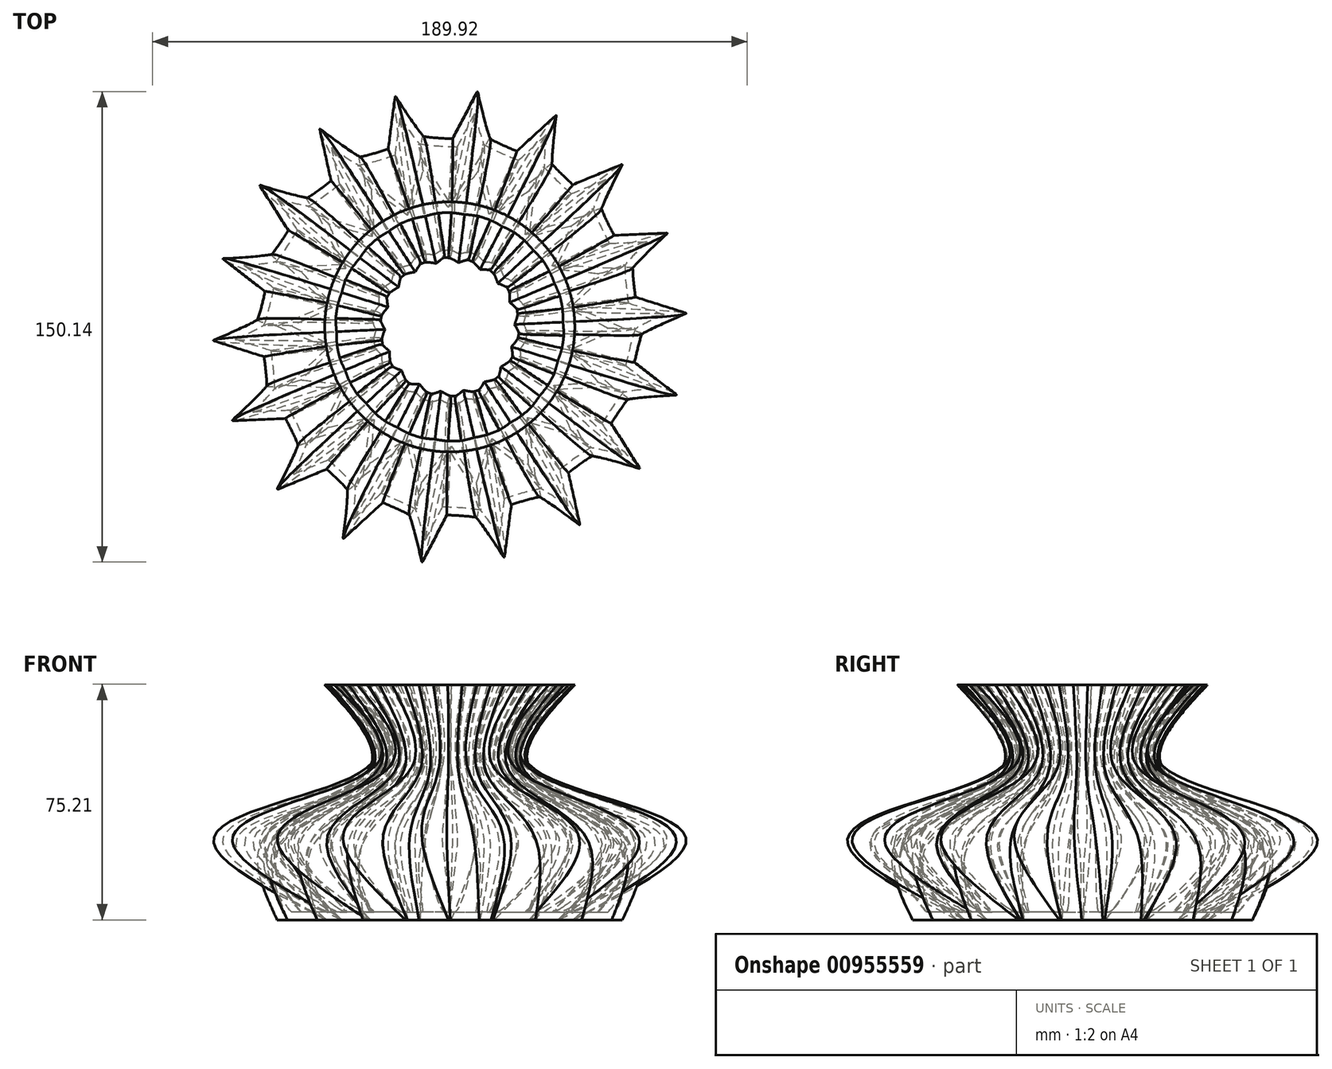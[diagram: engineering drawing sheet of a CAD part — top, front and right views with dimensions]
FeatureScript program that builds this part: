
annotation { "Feature Type Name" : "Feature", "Feature Type Description" : "" }
export const myFeature = defineFeature(function(context is Context, id is Id, definition is map)
    precondition{}
    {
        {
            var Q0;
            Q0=qCreatedBy(makeId("Top.planeOp"),FACE);
            var sketch = newSketch(context, id + "F0", { "sketchPlane" : qUnion([Q0])});
            skCircle(sketch, "E0", {"center": v(0, 0) * mm, "radius": 40 * mm});
            skLineSegment(sketch, "E1", {"start": v(-13.84, 37.53) * mm, "end": v(-27.36, 47.83) * mm});
            skLineSegment(sketch, "E2", {"start": v(-27.36, 47.83) * mm, "end": v(-25.33, 30.96) * mm});
            skLineSegment(sketch, "E3.1.0", {"start": v(-25.84, 30.53) * mm, "end": v(-42.07, 35.59) * mm});
            skLineSegment(sketch, "E3.1.1", {"start": v(-42.07, 35.59) * mm, "end": v(-34.4, 20.42) * mm});
            skLineSegment(sketch, "E3.2.0", {"start": v(-34.73, 19.85) * mm, "end": v(-51.7, 19.05) * mm});
            skLineSegment(sketch, "E3.2.1", {"start": v(-51.7, 19.05) * mm, "end": v(-39.3, 7.43) * mm});
            skLineSegment(sketch, "E3.3.0", {"start": v(-39.42, 6.78) * mm, "end": v(-55.1, 0.22) * mm});
            skLineSegment(sketch, "E3.3.1", {"start": v(-55.1, 0.22) * mm, "end": v(-39.47, -6.46) * mm});
            skLineSegment(sketch, "E3.4.0", {"start": v(-39.36, -7.12) * mm, "end": v(-51.86, -18.64) * mm});
            skLineSegment(sketch, "E3.4.1", {"start": v(-51.86, -18.64) * mm, "end": v(-34.88, -19.57) * mm});
            skLineSegment(sketch, "E3.5.0", {"start": v(-34.55, -20.15) * mm, "end": v(-42.36, -35.25) * mm});
            skLineSegment(sketch, "E3.5.1", {"start": v(-42.36, -35.25) * mm, "end": v(-26.09, -30.32) * mm});
            skLineSegment(sketch, "E3.6.0", {"start": v(-25.58, -30.75) * mm, "end": v(-27.74, -47.61) * mm});
            skLineSegment(sketch, "E3.6.1", {"start": v(-27.74, -47.61) * mm, "end": v(-14.14, -37.42) * mm});
            skLineSegment(sketch, "E3.7.0", {"start": v(-13.52, -37.65) * mm, "end": v(-9.78, -54.23) * mm});
            skLineSegment(sketch, "E3.7.1", {"start": v(-9.78, -54.23) * mm, "end": v(-0.5, -40) * mm});
            skLineSegment(sketch, "E3.8.0", {"start": v(0.17, -40) * mm, "end": v(9.35, -54.3) * mm});
            skLineSegment(sketch, "E3.8.1", {"start": v(9.35, -54.3) * mm, "end": v(13.22, -37.75) * mm});
            skLineSegment(sketch, "E3.9.0", {"start": v(13.84, -37.53) * mm, "end": v(27.36, -47.83) * mm});
            skLineSegment(sketch, "E3.9.1", {"start": v(27.36, -47.83) * mm, "end": v(25.33, -30.96) * mm});
            skLineSegment(sketch, "E3.10.0", {"start": v(25.84, -30.53) * mm, "end": v(42.07, -35.59) * mm});
            skLineSegment(sketch, "E3.10.1", {"start": v(42.07, -35.59) * mm, "end": v(34.4, -20.42) * mm});
            skLineSegment(sketch, "E3.11.0", {"start": v(34.73, -19.85) * mm, "end": v(51.7, -19.05) * mm});
            skLineSegment(sketch, "E3.11.1", {"start": v(51.7, -19.05) * mm, "end": v(39.3, -7.43) * mm});
            skLineSegment(sketch, "E3.12.0", {"start": v(39.42, -6.78) * mm, "end": v(55.1, -0.22) * mm});
            skLineSegment(sketch, "E3.12.1", {"start": v(55.1, -0.22) * mm, "end": v(39.47, 6.46) * mm});
            skLineSegment(sketch, "E3.13.0", {"start": v(39.36, 7.12) * mm, "end": v(51.86, 18.64) * mm});
            skLineSegment(sketch, "E3.13.1", {"start": v(51.86, 18.64) * mm, "end": v(34.88, 19.57) * mm});
            skLineSegment(sketch, "E3.14.0", {"start": v(34.55, 20.15) * mm, "end": v(42.36, 35.25) * mm});
            skLineSegment(sketch, "E3.14.1", {"start": v(42.36, 35.25) * mm, "end": v(26.09, 30.32) * mm});
            skLineSegment(sketch, "E3.15.0", {"start": v(25.58, 30.75) * mm, "end": v(27.74, 47.61) * mm});
            skLineSegment(sketch, "E3.15.1", {"start": v(27.74, 47.61) * mm, "end": v(14.14, 37.42) * mm});
            skLineSegment(sketch, "E3.16.0", {"start": v(13.52, 37.65) * mm, "end": v(9.78, 54.23) * mm});
            skLineSegment(sketch, "E3.16.1", {"start": v(9.78, 54.23) * mm, "end": v(0.5, 40) * mm});
            skLineSegment(sketch, "E3.17.0", {"start": v(-0.17, 40) * mm, "end": v(-9.35, 54.3) * mm});
            skLineSegment(sketch, "E3.17.1", {"start": v(-9.35, 54.3) * mm, "end": v(-13.22, 37.75) * mm});
            skSolve(sketch);
        }
        {
            var Q0;
            Q0=qCreatedBy(makeId("Top.planeOp"),FACE);
            var Q1;
            Q1 = qBodyType(qCreatedBy(id + "F2" ,EDGE), BodyType.WIRE);
            cPlane(context, id + "F1", {"entities" : qUnion([Q0, Q1]), "cplaneType" : CPlaneType.OFFSET, "offset" : 25 * mm, "width" : 150 * mm, "height" : 150 * mm});
        }
        {
            var Q0;
            Q0=qCreatedBy(id+"F1.planeOp",FACE);
            var sketch = newSketch(context, id + "F2", { "sketchPlane" : qUnion([Q0])});
            skCircle(sketch, "E4", {"center": v(0, 0) * mm, "radius": 60 * mm});
            skLineSegment(sketch, "E5", {"start": v(-27.72, 53.21) * mm, "end": v(-41.5, 63.16) * mm});
            skLineSegment(sketch, "E6", {"start": v(-41.5, 63.16) * mm, "end": v(-37.84, 46.56) * mm});
            skLineSegment(sketch, "E7.1.0", {"start": v(-44.25, 40.52) * mm, "end": v(-60.6, 45.16) * mm});
            skLineSegment(sketch, "E7.1.1", {"start": v(-60.6, 45.16) * mm, "end": v(-51.48, 30.81) * mm});
            skLineSegment(sketch, "E7.2.0", {"start": v(-55.44, 22.95) * mm, "end": v(-72.4, 21.7) * mm});
            skLineSegment(sketch, "E7.2.1", {"start": v(-72.4, 21.7) * mm, "end": v(-58.92, 11.34) * mm});
            skLineSegment(sketch, "E7.3.0", {"start": v(-59.94, 2.6) * mm, "end": v(-75.45, -4.36) * mm});
            skLineSegment(sketch, "E7.3.1", {"start": v(-75.45, -4.36) * mm, "end": v(-59.24, -9.5) * mm});
            skLineSegment(sketch, "E7.4.0", {"start": v(-57.22, -18.06) * mm, "end": v(-69.41, -29.9) * mm});
            skLineSegment(sketch, "E7.4.1", {"start": v(-69.41, -29.9) * mm, "end": v(-52.43, -29.18) * mm});
            skLineSegment(sketch, "E7.5.0", {"start": v(-47.6, -36.54) * mm, "end": v(-55, -51.84) * mm});
            skLineSegment(sketch, "E7.5.1", {"start": v(-55, -51.84) * mm, "end": v(-39.28, -45.35) * mm});
            skLineSegment(sketch, "E7.6.0", {"start": v(-32.23, -50.61) * mm, "end": v(-33.95, -67.52) * mm});
            skLineSegment(sketch, "E7.6.1", {"start": v(-33.95, -67.52) * mm, "end": v(-21.4, -56.05) * mm});
            skLineSegment(sketch, "E7.7.0", {"start": v(-12.97, -58.58) * mm, "end": v(-8.8, -75.06) * mm});
            skLineSegment(sketch, "E7.7.1", {"start": v(-8.8, -75.06) * mm, "end": v(-0.94, -60) * mm});
            skLineSegment(sketch, "E7.8.0", {"start": v(7.85, -59.48) * mm, "end": v(17.4, -73.55) * mm});
            skLineSegment(sketch, "E7.8.1", {"start": v(17.4, -73.55) * mm, "end": v(19.63, -56.7) * mm});
            skLineSegment(sketch, "E7.9.0", {"start": v(27.72, -53.21) * mm, "end": v(41.5, -63.16) * mm});
            skLineSegment(sketch, "E7.9.1", {"start": v(41.5, -63.16) * mm, "end": v(37.84, -46.56) * mm});
            skLineSegment(sketch, "E7.10.0", {"start": v(44.25, -40.52) * mm, "end": v(60.6, -45.16) * mm});
            skLineSegment(sketch, "E7.10.1", {"start": v(60.6, -45.16) * mm, "end": v(51.48, -30.81) * mm});
            skLineSegment(sketch, "E7.11.0", {"start": v(55.44, -22.95) * mm, "end": v(72.4, -21.7) * mm});
            skLineSegment(sketch, "E7.11.1", {"start": v(72.4, -21.7) * mm, "end": v(58.92, -11.34) * mm});
            skLineSegment(sketch, "E7.12.0", {"start": v(59.94, -2.6) * mm, "end": v(75.45, 4.36) * mm});
            skLineSegment(sketch, "E7.12.1", {"start": v(75.45, 4.36) * mm, "end": v(59.24, 9.5) * mm});
            skLineSegment(sketch, "E7.13.0", {"start": v(57.22, 18.06) * mm, "end": v(69.41, 29.9) * mm});
            skLineSegment(sketch, "E7.13.1", {"start": v(69.41, 29.9) * mm, "end": v(52.43, 29.18) * mm});
            skLineSegment(sketch, "E7.14.0", {"start": v(47.6, 36.54) * mm, "end": v(55, 51.84) * mm});
            skLineSegment(sketch, "E7.14.1", {"start": v(55, 51.84) * mm, "end": v(39.28, 45.35) * mm});
            skLineSegment(sketch, "E7.15.0", {"start": v(32.23, 50.61) * mm, "end": v(33.95, 67.52) * mm});
            skLineSegment(sketch, "E7.15.1", {"start": v(33.95, 67.52) * mm, "end": v(21.4, 56.05) * mm});
            skLineSegment(sketch, "E7.16.0", {"start": v(12.97, 58.58) * mm, "end": v(8.8, 75.06) * mm});
            skLineSegment(sketch, "E7.16.1", {"start": v(8.8, 75.06) * mm, "end": v(0.94, 60) * mm});
            skLineSegment(sketch, "E7.17.0", {"start": v(-7.85, 59.48) * mm, "end": v(-17.4, 73.55) * mm});
            skLineSegment(sketch, "E7.17.1", {"start": v(-17.4, 73.55) * mm, "end": v(-19.63, 56.7) * mm});
            skSolve(sketch);
        }
        {
            var Q0;
            Q0=qCreatedBy(id+"F1.planeOp",FACE);
            cPlane(context, id + "F3", {"entities" : qUnion([Q0]), "cplaneType" : CPlaneType.OFFSET, "offset" : 25 * mm, "width" : 150 * mm, "height" : 150 * mm});
        }
        {
            var Q0;
            Q0=qCreatedBy(id+"F3.planeOp",FACE);
            var sketch = newSketch(context, id + "F4", { "sketchPlane" : qUnion([Q0])});
            skCircle(sketch, "E8", {"center": v(0, 0) * mm, "radius": 25 * mm});
            skSolve(sketch);
        }
        {
            var Q0;
            Q0=qCreatedBy(id+"F3.planeOp",FACE);
            cPlane(context, id + "F5", {"entities" : qUnion([Q0]), "cplaneType" : CPlaneType.OFFSET, "offset" : 25 * mm, "width" : 150 * mm, "height" : 150 * mm});
        }
        {
            var Q0;
            Q0=qCreatedBy(id+"F5.planeOp",FACE);
            var sketch = newSketch(context, id + "F6", { "sketchPlane" : qUnion([Q0])});
            skCircle(sketch, "E9", {"center": v(0, 0) * mm, "radius": 39.91 * mm});
            skSolve(sketch);
        }
        {
            var Q0;
            Q0 = qSketchRegion(id + "F0", true);
            var Q1;
            Q1 = qSketchRegion(id + "F2", true);
            var Q2;
            Q2 = qSketchRegion(id + "F4", true);
            var Q3;
            Q3 = qSketchRegion(id + "F6", true);
            loft(context, id + "F7", {"sheetProfilesArray" : [{ "sheetProfileEntities" : qUnion([Q0]) }, { "sheetProfileEntities" : qUnion([Q1]) }, { "sheetProfileEntities" : qUnion([Q2]) }, { "sheetProfileEntities" : qUnion([Q3]) }]});
        }
        {
            var Q0;
            Q0=makeQuery(id+"F7.opLoft","CAP_FACE",FACE,{"disambiguationData":[OSD([makeQuery(id+"F6.imprint","IMPRINT",FACE,{"disambiguationData":[TD([[makeQuery(id+"F6.imprint","IMPRINT",EDGE,{"derivedFrom":sQuery(id+"F6.wireOp",EDGE,"E9")}),1.0]])]})])],"isStart":true});
            shell(context, id + "F8", {"entities" : qUnion([Q0]), "thickness" : 2.5 * mm});
        }
    });
